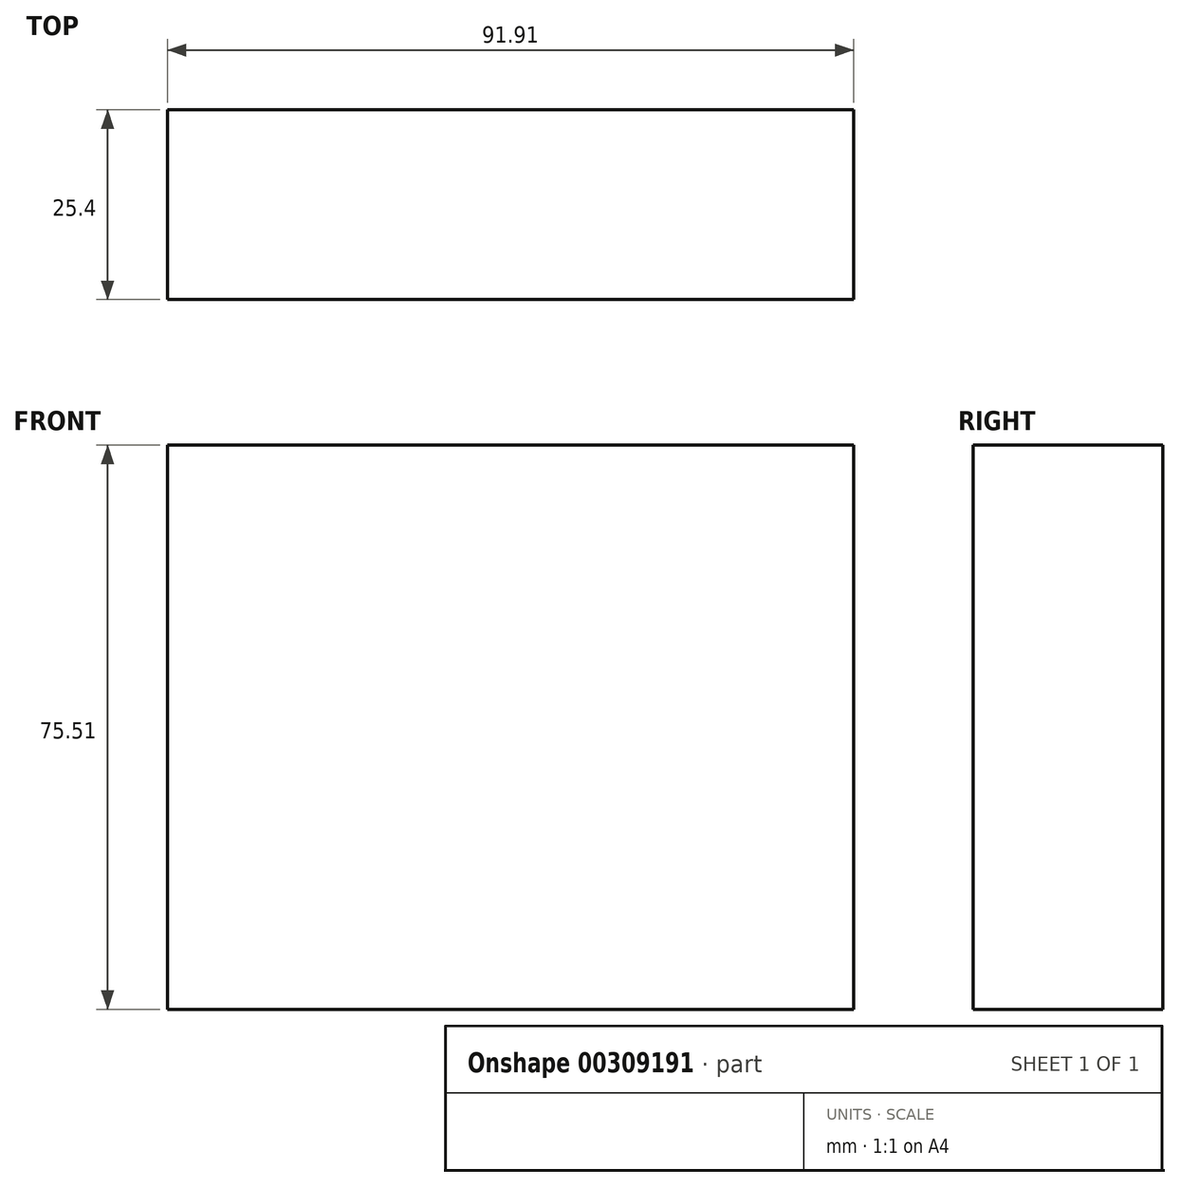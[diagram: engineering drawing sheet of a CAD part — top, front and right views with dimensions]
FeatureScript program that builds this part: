
annotation { "Feature Type Name" : "Feature", "Feature Type Description" : "" }
export const myFeature = defineFeature(function(context is Context, id is Id, definition is map)
    precondition{}
    {
        {
            var Q0;
            Q0=qCreatedBy(makeId("Front.planeOp"),FACE);
            var sketch = newSketch(context, id + "F0", { "sketchPlane" : qUnion([Q0])});
            skLineSegment(sketch, "E0.bottom", {"start": v(-57.9, 37.02) * mm, "end": v(34.01, 37.02) * mm});
            skLineSegment(sketch, "E0.top", {"start": v(-57.9, -38.49) * mm, "end": v(34.01, -38.49) * mm});
            skLineSegment(sketch, "E0.left", {"start": v(-57.9, 37.02) * mm, "end": v(-57.9, -38.49) * mm});
            skLineSegment(sketch, "E0.right", {"start": v(34.01, 37.02) * mm, "end": v(34.01, -38.49) * mm});
            skSolve(sketch);
        }
        {
            var Q0;
            Q0 = qSketchRegion(id + "F0", true);
            extrude(context, id + "F1", {"entities" : qUnion([Q0]), "depth" : 25.4 * mm});
        }
    });
